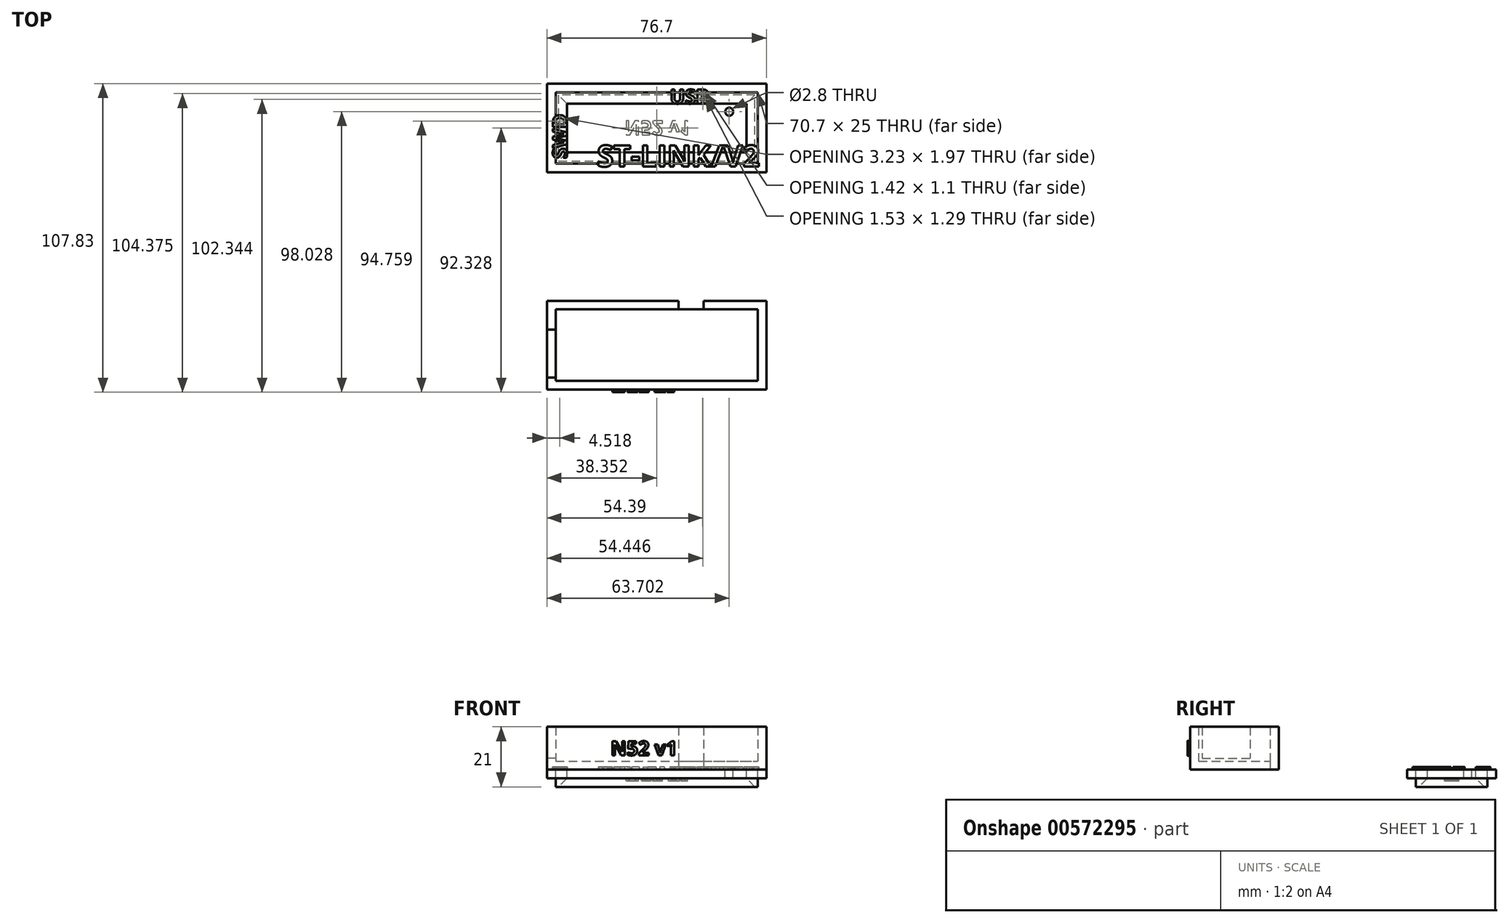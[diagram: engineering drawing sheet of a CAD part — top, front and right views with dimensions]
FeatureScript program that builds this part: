
annotation { "Feature Type Name" : "Feature", "Feature Type Description" : "" }
export const myFeature = defineFeature(function(context is Context, id is Id, definition is map)
    precondition{}
    {
        {
            var Q0;
            Q0=qCreatedBy(makeId("Top.planeOp"),FACE);
            var sketch = newSketch(context, id + "F0", { "sketchPlane" : qUnion([Q0])});
            skLineSegment(sketch, "E0.bottom", {"start": v(-30.55, -12.21) * mm, "end": v(40.15, -12.21) * mm});
            skLineSegment(sketch, "E0.top", {"start": v(-30.55, 12.79) * mm, "end": v(40.15, 12.79) * mm});
            skLineSegment(sketch, "E0.left", {"start": v(-30.55, -12.21) * mm, "end": v(-30.55, 12.79) * mm});
            skLineSegment(sketch, "E0.right", {"start": v(40.15, -12.21) * mm, "end": v(40.15, 12.79) * mm});
            skLineSegment(sketch, "E1.bottom", {"start": v(21.15, 12.79) * mm, "end": v(12.45, 12.79) * mm});
            skLineSegment(sketch, "E1.top", {"start": v(21.15, 15.79) * mm, "end": v(12.45, 15.79) * mm});
            skLineSegment(sketch, "E1.left", {"start": v(21.15, 12.79) * mm, "end": v(21.15, 15.79) * mm});
            skLineSegment(sketch, "E1.right", {"start": v(12.45, 12.79) * mm, "end": v(12.45, 15.79) * mm});
            skLineSegment(sketch, "E2", {"start": v(12.45, 15.79) * mm, "end": v(-33.55, 15.79) * mm});
            skLineSegment(sketch, "E3", {"start": v(-33.55, 15.79) * mm, "end": v(-33.55, -15.21) * mm});
            skLineSegment(sketch, "E4", {"start": v(-33.55, -15.21) * mm, "end": v(43.15, -15.21) * mm});
            skLineSegment(sketch, "E5", {"start": v(43.15, -15.21) * mm, "end": v(43.15, 15.79) * mm});
            skLineSegment(sketch, "E6", {"start": v(43.15, 15.79) * mm, "end": v(21.15, 15.79) * mm});
            skLineSegment(sketch, "E7", {"start": v(-33.55, 5.79) * mm, "end": v(-30.55, 5.79) * mm});
            skLineSegment(sketch, "E8", {"start": v(-30.55, -11.01) * mm, "end": v(-33.55, -11.01) * mm});
            skLineSegment(sketch, "E9.bottom", {"start": v(43.15, 60.72) * mm, "end": v(-33.55, 60.72) * mm});
            skLineSegment(sketch, "E9.top", {"start": v(43.15, 91.72) * mm, "end": v(-33.55, 91.72) * mm});
            skLineSegment(sketch, "E9.left", {"start": v(43.15, 60.72) * mm, "end": v(43.15, 91.72) * mm});
            skLineSegment(sketch, "E9.right", {"start": v(-33.55, 60.72) * mm, "end": v(-33.55, 91.72) * mm});
            skLineSegment(sketch, "E10.bottom", {"start": v(40.15, 63.72) * mm, "end": v(-30.55, 63.72) * mm});
            skLineSegment(sketch, "E10.top", {"start": v(40.15, 88.72) * mm, "end": v(-30.55, 88.72) * mm});
            skLineSegment(sketch, "E10.left", {"start": v(40.15, 63.72) * mm, "end": v(40.15, 88.72) * mm});
            skLineSegment(sketch, "E10.right", {"start": v(-30.55, 63.72) * mm, "end": v(-30.55, 88.72) * mm});
            skLineSegment(sketch, "E11.bottom", {"start": v(-26.55, 84.72) * mm, "end": v(36.15, 84.72) * mm});
            skLineSegment(sketch, "E11.top", {"start": v(-26.55, 67.72) * mm, "end": v(36.15, 67.72) * mm});
            skLineSegment(sketch, "E11.left", {"start": v(-26.55, 84.72) * mm, "end": v(-26.55, 67.72) * mm});
            skLineSegment(sketch, "E11.right", {"start": v(36.15, 84.72) * mm, "end": v(36.15, 67.72) * mm});
            skPoint(sketch, "E12", {"position": v(16.8, 15.79) * mm});
            skLineSegment(sketch, "E13", {"start": v(-33.55, 5.79) * mm, "end": v(-33.55, -11.01) * mm});
            skPoint(sketch, "E14", {"position": v(-33.55, -2.61) * mm});
            skSolve(sketch);
        }
        {
            var Q0;
            Q0=makeQuery(id+"F0.imprint","IMPRINT",FACE,{"disambiguationData":[TD([[makeQuery(id+"F0.imprint","IMPRINT",EDGE,{"derivedFrom":sQuery(id+"F0.wireOp",EDGE,"E0.bottom")}),1.0]])]});
            extrude(context, id + "F1", {"entities" : qUnion([Q0]), "depth" : 3 * mm, "offsetDistance" : 25 * mm});
        }
        {
            var Q0;
            {var subQ0=sQuery(id+"F0.wireOp",EDGE,"E1.right");Q0=makeQuery(id+"F0.imprint","IMPRINT",FACE,{"disambiguationData":[TD([[makeQuery(id+"F0.imprint","IMPRINT",EDGE,{"derivedFrom":subQ0}),1.0]])]});}
            var Q1;
            {var subQ2=sQuery(id+"F0.wireOp",EDGE,"E0.bottom");Q1=makeQuery(id+"F0.imprint","IMPRINT",FACE,{"disambiguationData":[TD([[makeQuery(id+"F0.imprint","IMPRINT",EDGE,{"derivedFrom":subQ2}),-1.0]])]});}
            extrude(context, id + "F2", {"entities" : qUnion([Q0, Q1]), "operationType" : NewBodyOperationType.ADD, "depth" : 15 * mm, "offsetDistance" : 25 * mm});
        }
        {
            var Q0;
            Q0=makeQuery(id+"F0.imprint","IMPRINT",FACE,{"disambiguationData":[TD([[makeQuery(id+"F0.imprint","IMPRINT",EDGE,{"derivedFrom":sQuery(id+"F0.wireOp",EDGE,"E1.bottom")}),-1.0]])]});
            var Q1;
            {var subQ0=sQuery(id+"F0.wireOp",EDGE,"E7");Q1=makeQuery(id+"F0.imprint","IMPRINT",FACE,{"disambiguationData":[TD([[makeQuery(id+"F0.imprint","IMPRINT",EDGE,{"derivedFrom":subQ0}),-1.0]])]});}
            extrude(context, id + "F3", {"entities" : qUnion([Q0, Q1]), "operationType" : NewBodyOperationType.ADD, "depth" : 4 * mm, "offsetDistance" : 25 * mm});
        }
        {
            var Q0;
            Q0=makeQuery(id+"F0.imprint","IMPRINT",FACE,{"disambiguationData":[TD([[makeQuery(id+"F0.imprint","IMPRINT",EDGE,{"derivedFrom":sQuery(id+"F0.wireOp",EDGE,"E9.bottom")}),-1.0]])]});
            var Q1;
            Q1=makeQuery(id+"F0.imprint","IMPRINT",FACE,{"disambiguationData":[TD([[makeQuery(id+"F0.imprint","IMPRINT",EDGE,{"derivedFrom":sQuery(id+"F0.wireOp",EDGE,"E11.bottom")}),-1.0]])]});
            extrude(context, id + "F4", {"entities" : qUnion([Q0, Q1]), "oppositeDirection" : true, "depth" : 3 * mm, "offsetDistance" : 25 * mm});
        }
        {
            var Q0;
            Q0=makeQuery(id+"F0.imprint","IMPRINT",FACE,{"disambiguationData":[TD([[makeQuery(id+"F0.imprint","IMPRINT",EDGE,{"derivedFrom":sQuery(id+"F0.wireOp",EDGE,"E10.bottom")}),-1.0]])]});
            extrude(context, id + "F5", {"entities" : qUnion([Q0]), "oppositeDirection" : true, "depth" : 6 * mm, "offsetDistance" : 25 * mm});
        }
        {
            var Q0;
            Q0=makeQuery(id+"F5.opExtrude","CAP_EDGE",EDGE,{"disambiguationData":[OSD([sQuery(id+"F0.wireOp",EDGE,"E11.left")])],"isStart":false});
            var Q1;
            Q1=makeQuery(id+"F5.opExtrude","CAP_EDGE",EDGE,{"disambiguationData":[OSD([sQuery(id+"F0.wireOp",EDGE,"E11.bottom")])],"isStart":false});
            var Q2;
            Q2=makeQuery(id+"F5.opExtrude","CAP_EDGE",EDGE,{"disambiguationData":[OSD([sQuery(id+"F0.wireOp",EDGE,"E11.top")])],"isStart":false});
            var Q3;
            Q3=makeQuery(id+"F5.opExtrude","CAP_EDGE",EDGE,{"disambiguationData":[OSD([sQuery(id+"F0.wireOp",EDGE,"E11.right")])],"isStart":false});
            chamfer(context, id + "F6", {"entities" : qUnion([Q0, Q1, Q2, Q3]), "width" : 3 * mm, "tangentPropagation" : true});
        }
        {
            var Q0;
            Q0=makeQuery(id+"F0.imprint","IMPRINT",FACE,{"disambiguationData":[TD([[makeQuery(id+"F0.imprint","IMPRINT",EDGE,{"derivedFrom":sQuery(id+"F0.wireOp",EDGE,"E9.bottom")}),-1.0]])]});
            var sketch = newSketch(context, id + "F7", { "sketchPlane" : qUnion([Q0])});
            skPoint(sketch, "E15.0", {"position": v(16.8, 15.79) * mm});
            skPoint(sketch, "E16.0", {"position": v(-33.55, -2.61) * mm});
            skText(sketch, "E17", { "text": "ST-LINK/V2", "fontName": "OpenSans-Bold.ttf"});
            skText(sketch, "E18", { "text": "USB", "fontName": "OpenSans-Bold.ttf"});
            skText(sketch, "E19", { "text": "SWD", "fontName": "OpenSans-Bold.ttf"});
            skCircle(sketch, "E20", {"center": v(30.15, 81.92) * mm, "radius": 1.4 * mm});
            const initialGuessF7  = {"E17": [-0.01605, 0.06272, 1, 0, 0.0075], "E18": [0.00938, 0.08472, 1, 0, 0.005], "E19": [-0.02655, 0.06545, 0, 1, 0.005]};
            skSetInitialGuess(sketch, initialGuessF7);
            skSolve(sketch);
        }
        {
            var Q0;
            Q0 = qSketchRegion(id + "F7", true);
            extrude(context, id + "F8", {"entities" : qUnion([Q0]), "depth" : 0.9 * mm, "offsetDistance" : 25 * mm});
        }
        {
            var Q0;
            Q0=makeQuery(id+"F8.opExtrude","CAP_FACE",FACE,{"disambiguationData":[OSD([sQuery(id+"F7.wireOp",EDGE,"E20")])],"isStart":false});
            extrude(context, id + "F9", {"entities" : qUnion([Q0]), "operationType" : NewBodyOperationType.REMOVE, "endBound" : BoundingType.THROUGH_ALL, "oppositeDirection" : true, "depth" : 25 * mm, "offsetDistance" : 25 * mm});
        }
        {
            var Q0;
            Q0=makeQuery(id+"F4.opExtrude","CAP_FACE",FACE,{"disambiguationData":[OSD([sQuery(id+"F0.wireOp",EDGE,"E11.bottom"),sQuery(id+"F0.wireOp",EDGE,"E11.top"),sQuery(id+"F0.wireOp",EDGE,"E11.left"),sQuery(id+"F0.wireOp",EDGE,"E11.right")])],"isStart":false});
            var sketch = newSketch(context, id + "F10", { "sketchPlane" : qUnion([Q0])});
            skText(sketch, "E21", { "text": "N52 v1", "fontName": "OpenSans-Bold.ttf"});
            const initialGuessF10  = {"E21": [-0.00652, -0.07872, 1, 0, 0.005]};
            skSetInitialGuess(sketch, initialGuessF10);
            skSolve(sketch);
        }
        {
            var Q0;
            Q0 = qSketchRegion(id + "F10", true);
            extrude(context, id + "F11", {"entities" : qUnion([Q0]), "operationType" : NewBodyOperationType.ADD, "depth" : 0.9 * mm, "offsetDistance" : 25 * mm});
        }
        {
            var Q0;
            Q0=makeQuery(id+"F2.opExtrude","SWEPT_FACE",FACE,{"disambiguationData":[OSD([sQuery(id+"F0.wireOp",EDGE,"E4")])]});
            var sketch = newSketch(context, id + "F12", { "sketchPlane" : qUnion([Q0])});
            skText(sketch, "E22", { "text": "N52 v1", "fontName": "OpenSans-Bold.ttf"});
            const initialGuessF12  = {"E22": [-0.01132, 0.005, 1, 0, 0.005]};
            skSetInitialGuess(sketch, initialGuessF12);
            skSolve(sketch);
        }
        {
            var Q0;
            Q0 = qSketchRegion(id + "F12", true);
            extrude(context, id + "F13", {"entities" : qUnion([Q0]), "operationType" : NewBodyOperationType.ADD, "depth" : 0.9 * mm, "offsetDistance" : 25 * mm});
        }
    });
